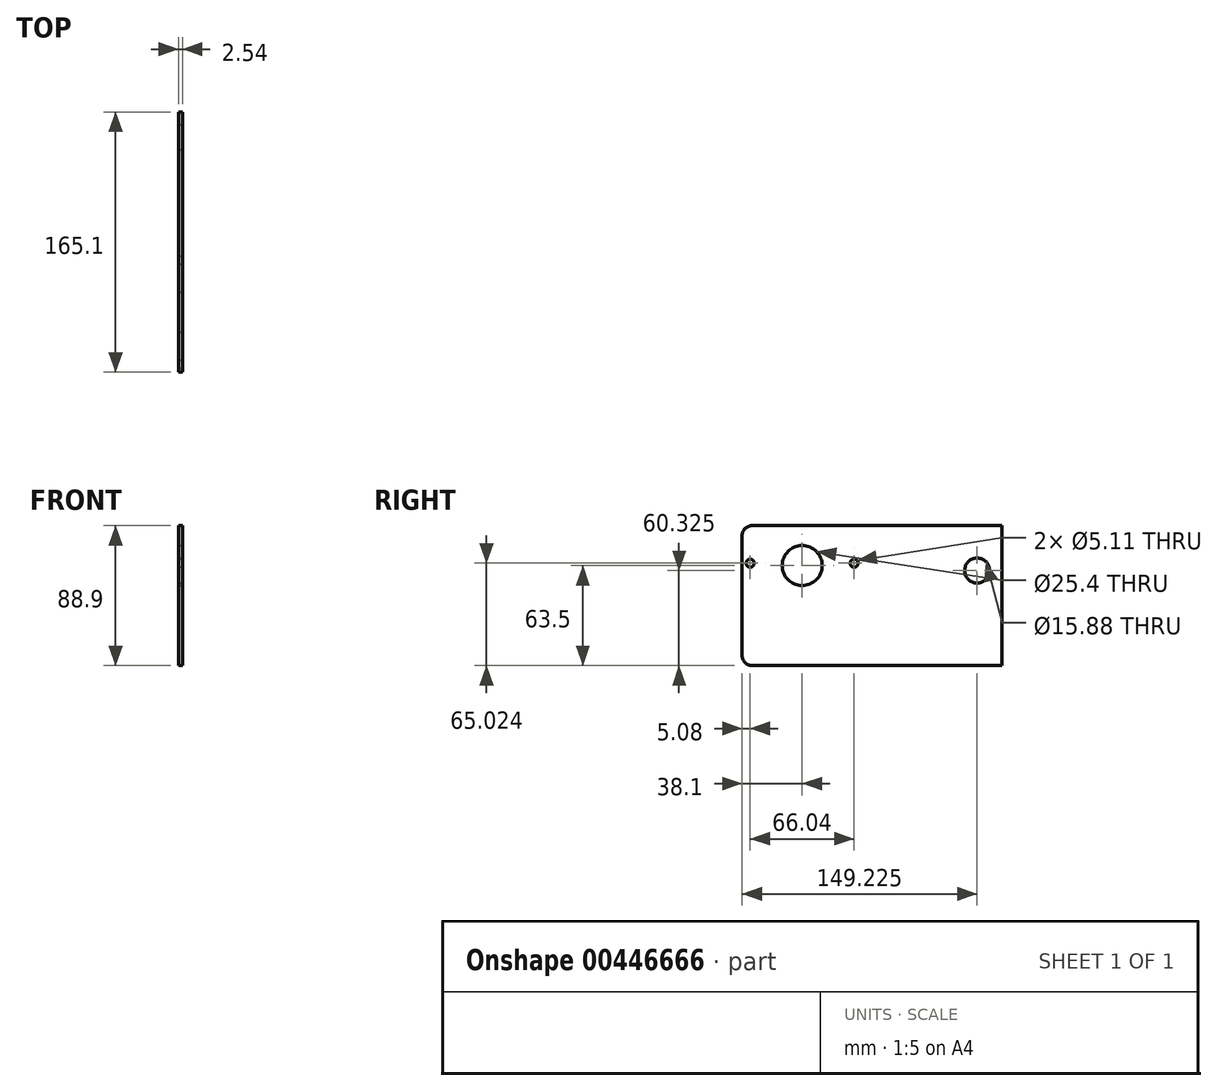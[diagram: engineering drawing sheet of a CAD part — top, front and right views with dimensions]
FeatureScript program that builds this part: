
annotation { "Feature Type Name" : "Feature", "Feature Type Description" : "" }
export const myFeature = defineFeature(function(context is Context, id is Id, definition is map)
    precondition{}
    {
        {
            var Q0;
            Q0=qCreatedBy(makeId("Right.planeOp"),FACE);
            var sketch = newSketch(context, id + "F0", { "sketchPlane" : qUnion([Q0])});
            skLineSegment(sketch, "E0.bottom", {"start": v(6.35, 0) * mm, "end": v(165.1, 0) * mm});
            skLineSegment(sketch, "E0.top", {"start": v(6.35, 88.9) * mm, "end": v(165.1, 88.9) * mm});
            skLineSegment(sketch, "E0.left", {"start": v(0, 6.35) * mm, "end": v(0, 82.55) * mm});
            skLineSegment(sketch, "E0.right", {"start": v(165.1, 0) * mm, "end": v(165.1, 88.9) * mm});
            skPoint(sketch, "E1.visualSharp", {"position": v(0, 88.9) * mm});
            skArc(sketch, "E1.filletArc", {"start": v(6.35, 88.9) * mm, "mid": v(1.86, 87.04) * mm, "end": v(0, 82.55) * mm});
            skPoint(sketch, "E2.visualSharp", {"position": v(0, 0) * mm});
            skArc(sketch, "E2.filletArc", {"start": v(0, 6.35) * mm, "mid": v(1.86, 1.86) * mm, "end": v(6.35, 0) * mm});
            skSolve(sketch);
        }
        {
            var Q0;
            Q0=makeQuery(id+"F0.imprint","IMPRINT",FACE,{"disambiguationData":[TD([[makeQuery(id+"F0.imprint","IMPRINT",EDGE,{"derivedFrom":sQuery(id+"F0.wireOp",EDGE,"E0.bottom")}),1.0]])]});
            extrude(context, id + "F1", {"entities" : qUnion([Q0]), "depth" : 2.54 * mm, "offsetDistance" : 25.4 * mm});
        }
        {
            var Q0;
            Q0=makeQuery(id+"F1.opExtrude","CAP_FACE",FACE,{"disambiguationData":[OSD([sQuery(id+"F0.wireOp",EDGE,"E0.bottom"),sQuery(id+"F0.wireOp",EDGE,"E0.top"),sQuery(id+"F0.wireOp",EDGE,"E0.left"),sQuery(id+"F0.wireOp",EDGE,"E0.right")])],"isStart":false});
            var sketch = newSketch(context, id + "F2", { "sketchPlane" : qUnion([Q0])});
            skLineSegment(sketch, "E3.0", {"start": v(0, 63.5) * mm, "end": v(114.3, 63.5) * mm, "construction": true});
            skLineSegment(sketch, "E4.0", {"start": v(38.1, 0) * mm, "end": v(38.1, 101.6) * mm, "construction": true});
            skPoint(sketch, "E5", {"position": v(38.1, 63.5) * mm});
            skCircle(sketch, "E6", {"center": v(38.1, 63.5) * mm, "radius": 12.7 * mm});
            skLineSegment(sketch, "E7.0", {"start": v(149.22, 0) * mm, "end": v(149.22, 88.9) * mm, "construction": true});
            skLineSegment(sketch, "E8.0", {"start": v(6.35, 60.33) * mm, "end": v(165.1, 60.33) * mm, "construction": true});
            skPoint(sketch, "E9", {"position": v(149.22, 60.33) * mm});
            skCircle(sketch, "E10", {"center": v(149.22, 60.33) * mm, "radius": 7.94 * mm});
            skSolve(sketch);
        }
        {
            var Q0;
            Q0=makeQuery(id+"F2.imprint","IMPRINT",FACE,{"disambiguationData":[TD([[makeQuery(id+"F2.imprint","IMPRINT",EDGE,{"derivedFrom":sQuery(id+"F2.wireOp",EDGE,"8UxfRhlu-CV3w-seKx-E2um-E2GBoEzcIsnR")}),1.0]])]});
            var Q1;
            Q1=makeQuery(id+"F2.imprint","IMPRINT",FACE,{"disambiguationData":[TD([[makeQuery(id+"F2.imprint","IMPRINT",EDGE,{"derivedFrom":sQuery(id+"F2.wireOp",EDGE,"E6")}),1.0]])]});
            var Q2;
            Q2=sQuery(id+"F2.wireOp",EDGE,"8UxfRhlu-CV3w-seKx-E2um-E2GBoEzcIsnR");
            extrude(context, id + "F3", {"entities" : qUnion([Q0, Q1]), "operationType" : NewBodyOperationType.REMOVE, "surfaceEntities" : qUnion([Q2]), "endBound" : BoundingType.THROUGH_ALL, "oppositeDirection" : true, "depth" : 25.4 * mm, "offsetDistance" : 25.4 * mm});
        }
        {
            var Q0;
            Q0 = qSketchRegion(id + "F2", true);
            extrude(context, id + "F4", {"entities" : qUnion([Q0]), "operationType" : NewBodyOperationType.REMOVE, "oppositeDirection" : true, "depth" : 25.4 * mm, "offsetDistance" : 25.4 * mm});
        }
        {
            var Q0;
            Q0=makeQuery(id+"F1.opExtrude","CAP_FACE",FACE,{"disambiguationData":[OSD([sQuery(id+"F0.wireOp",EDGE,"E0.bottom"),sQuery(id+"F0.wireOp",EDGE,"E0.top"),sQuery(id+"F0.wireOp",EDGE,"E0.left"),sQuery(id+"F0.wireOp",EDGE,"E0.right"),sQuery(id+"F0.wireOp",EDGE,"E1.filletArc"),sQuery(id+"F0.wireOp",EDGE,"E2.filletArc")])],"isStart":false});
            var sketch = newSketch(context, id + "F5", { "sketchPlane" : qUnion([Q0])});
            skLineSegment(sketch, "E11", {"start": v(38.1, 63.5) * mm, "end": v(178.98, 63.5) * mm, "construction": true});
            skLineSegment(sketch, "E12.0", {"start": v(38.1, 65.02) * mm, "end": v(178.98, 65.02) * mm, "construction": true});
            skLineSegment(sketch, "E13", {"start": v(38.1, 65.02) * mm, "end": v(38.1, 22.96) * mm, "construction": true});
            skLineSegment(sketch, "E14.0", {"start": v(5.08, 65.02) * mm, "end": v(5.08, 22.96) * mm, "construction": true});
            skLineSegment(sketch, "E15.0", {"start": v(71.12, 65.02) * mm, "end": v(71.12, 22.96) * mm, "construction": true});
            skCircle(sketch, "E16", {"center": v(5.08, 65.02) * mm, "radius": 2.55 * mm});
            skCircle(sketch, "E17", {"center": v(-10.98, 65.02) * mm, "radius": 1.52 * mm, "construction": true});
            skCircle(sketch, "E18", {"center": v(71.12, 65.02) * mm, "radius": 2.55 * mm});
            skSolve(sketch);
        }
        {
            var Q0;
            Q0 = qSketchRegion(id + "F5", true);
            extrude(context, id + "F6", {"entities" : qUnion([Q0]), "operationType" : NewBodyOperationType.REMOVE, "oppositeDirection" : true, "depth" : 25.4 * mm, "offsetDistance" : 25.4 * mm});
        }
    });
